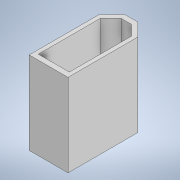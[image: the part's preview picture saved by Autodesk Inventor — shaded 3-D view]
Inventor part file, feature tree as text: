
AUTODESK INVENTOR PART (.ipt)
format: ipt  version: 2020 (Build 240168000, 168)  size: 112,640 bytes
history: native  units: mm
features: extrude x2, sketch x2
ambient origin geometry x8: Origin, YZ Plane, XZ Plane, XY Plane, X Axis, Y Axis, Z Axis, Center Point
bodies: Solid1 (feature_tree)
feature tree (4):
  extrude  "Extrusion1"  Depth=7.5mm
  extrude  "Extrusion2"  Depth=8.0mm
  sketch  "Sketch1"  dims[d0=7.5mm d1=3.75mm]
  sketch  "Sketch2"  dims[d2=16.0mm d3=8.0mm d4=2.5mm d5=135.0deg d6=135.0deg d7=16.0mm d8=0.0mm d9=14.0mm d10=2.0mm d11=7.0mm d12=6.0mm d13=3.0mm d14=8.0mm d15=0.0mm]
